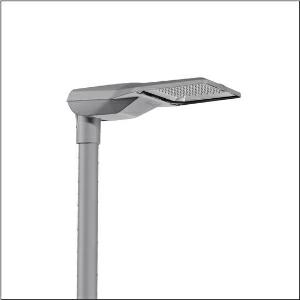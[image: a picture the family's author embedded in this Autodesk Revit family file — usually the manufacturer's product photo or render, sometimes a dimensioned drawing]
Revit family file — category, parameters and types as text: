
# Revit family: streetlight_sl_21_midi___st0_8a_5xe7c43a08mb_8186
name_source: partatom
category: Lighting Fixtures
units: mm (PartAtom-declared; Revit-internal decimal feet)

## family parameters
Cut with Voids When Loaded = No
Host = Face
Light Source = No
Part Type = Normal
Room Calculation Point = No
Round Connector Dimension = Use Diameter
Shared = No

## types (1)
- --- (1 x LED, 20180 lm, 147 W, 4000K)
    Apparent Load = 147 VA
    CIE Flux Codes = 38 75 97 100 100
    Color Rendering = 70
    Color Temperature = 4000K
    Default Elevation = 1800 mm
    Description = Streetlight SL 21 midi, mast luminaire, primary light control with lens, of PMMA, primary optical cover: cover, of toughened safety glass, transparent, light distribution: ST0.8a, light emission: direct distribution, primary light characteristic: asymmetric, installation type: post-top, side-entry, LED, 3G 1.5mm², High Power LED, rated luminous flux: 20.180lm, luminous efficacy: 137lm/W, light colour: 740, colour temperature: 4000K, control: overheat protection, constant luminous flux control, time-dependent luminous flux control, flexible luminous flux parameterisation, mains connection: 220..240V, AC, 50/60Hz, connection cable pre-assembled, cable length: 12,5m, wiring characteristics: H07RN-F, start of lifetime: 147W, end of service life: 155W, reduction: 64W, luminaire housing, of diecast aluminium, powder-coated, Siteco® metallic grey (DB 702S), corrosivity category C5 mid according to DIN EN ISO 12944, please order mast flange separately, inclination adjustable: 0°, 5°, 10°, 15°, sealing non-destructively replaceable, multi-level sealing system, length: 644mm, width: 335mm, height: 110mm, mast flange for spigot size: 42mm (side-entry): 5XC10008XM4, 60/48mm (side-entry/post-top): 5XC10108XM2, 76/60mm (side-entry/post-top): 5XC10108XM1, protection rating (complete): IP66, insulation class (complete): insulation class II (safety insulation), certification: CE, ENEC, ENEC+, VDE, impact resistance: IK09, permissible operating ambient temperature for outdoor applications: -40..+50°C, standard-compliant lighting for roads and squares, packaging unit: 1 piece

Light Distribution: ST0.8a
    Height = 111 mm
    Lamp = 1 x LED
    Lamp Light Flux = 20180 lm
    Lamp Power = 147 W
    Lamp count = 1
    Length = 644 mm
    Luminous efficacy = 137 lm/W
    Manufacturer = Siteco
    ModVariant = No
    Model = 5XE7C43A08MB
    Number of Poles = 1
    OnlyDefault = Yes
    Power Factor = 1
    Product Name = Streetlight SL 21 midi | ST0.8a
    Product group = mast luminaire | pylon top
    ProductGroupID = 6100
    Protection Class = Protection class II
    Protection Degree = IP 66
    RLX_Detail_Level = 1
    RLX_Emergency_Light_Flux = 0 lm
    RLX_Emergency_Type = 0
    RLX_Emergency_Type_DB = No
    RlxData = <blob elided: 90557 chars, md5=5092e882>
    Socket = socket
    Standby Power = 0 W
    System Light Flux = 20180 lm
    System Power = 147 W
    Type Comments = factory setting: luminous flux: 100 % | Output Level: 100 % | 750 mA
    Type Image = l_1004298.jpg
    URL = http://relux.com
    VarID = @adj_137357
    Voltage = 0 V
    Weight = 0.00 kg
    Width = 336 mm

## geometry (parser evidence)
native form markers: Blend x4, Sweep x12
no freeform markers — native parametric forms only
